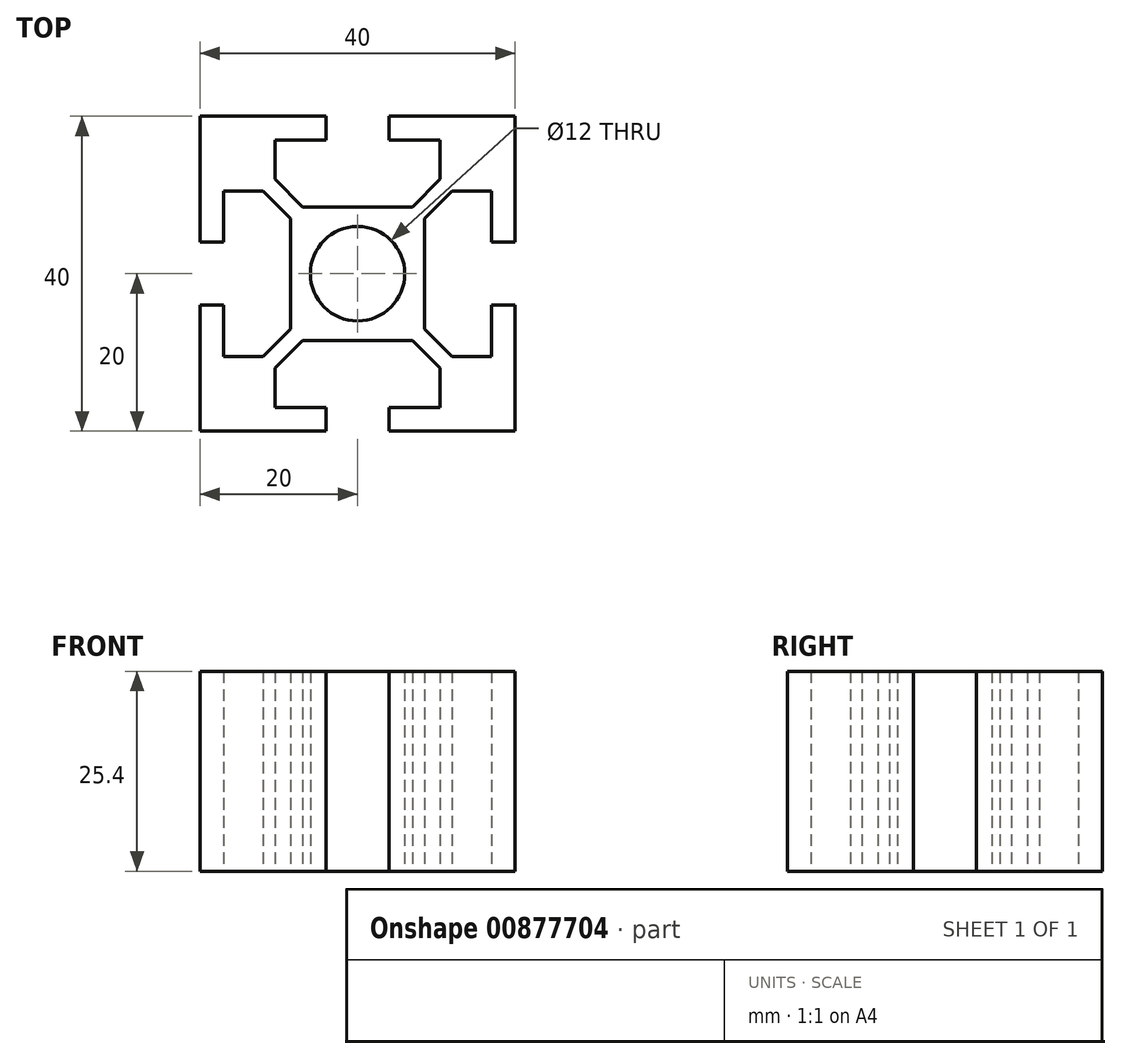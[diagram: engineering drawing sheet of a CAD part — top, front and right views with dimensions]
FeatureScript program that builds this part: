
annotation { "Feature Type Name" : "Feature", "Feature Type Description" : "" }
export const myFeature = defineFeature(function(context is Context, id is Id, definition is map)
    precondition{}
    {
        {
            var Q0;
            Q0=qCreatedBy(makeId("Top.planeOp"),FACE);
            var sketch = newSketch(context, id + "F0", { "sketchPlane" : qUnion([Q0])});
            skLineSegment(sketch, "E0", {"start": v(4, 17) * mm, "end": v(10.5, 17) * mm});
            skLineSegment(sketch, "E1", {"start": v(10.5, 17) * mm, "end": v(10.5, 12) * mm});
            skLineSegment(sketch, "E2", {"start": v(10.5, 12) * mm, "end": v(7, 8.5) * mm});
            skLineSegment(sketch, "E3", {"start": v(7, 8.5) * mm, "end": v(-7, 8.5) * mm});
            skLineSegment(sketch, "E4", {"start": v(-7, 8.5) * mm, "end": v(-10.5, 12) * mm});
            skLineSegment(sketch, "E5", {"start": v(-10.5, 12) * mm, "end": v(-10.5, 17) * mm});
            skLineSegment(sketch, "E6", {"start": v(-10.5, 17) * mm, "end": v(-4, 17) * mm});
            skLineSegment(sketch, "E7", {"start": v(-4, 17) * mm, "end": v(-4, 20) * mm});
            skLineSegment(sketch, "E8", {"start": v(-4, 20) * mm, "end": v(-20, 20) * mm});
            skLineSegment(sketch, "E9", {"start": v(-20, 20) * mm, "end": v(-20, 4) * mm});
            skLineSegment(sketch, "E10", {"start": v(-20, 4) * mm, "end": v(-17, 4) * mm});
            skLineSegment(sketch, "E11", {"start": v(-17, 4) * mm, "end": v(-17, 10.5) * mm});
            skLineSegment(sketch, "E12", {"start": v(-17, 10.5) * mm, "end": v(-12, 10.5) * mm});
            skLineSegment(sketch, "E13", {"start": v(-12, 10.5) * mm, "end": v(-8.5, 7) * mm});
            skLineSegment(sketch, "E14", {"start": v(-8.5, 7) * mm, "end": v(-8.5, -7) * mm});
            skLineSegment(sketch, "E15", {"start": v(-8.5, -7) * mm, "end": v(-12, -10.5) * mm});
            skLineSegment(sketch, "E16", {"start": v(-12, -10.5) * mm, "end": v(-17, -10.5) * mm});
            skLineSegment(sketch, "E17", {"start": v(-17, -10.5) * mm, "end": v(-17, -4) * mm});
            skLineSegment(sketch, "E18", {"start": v(-17, -4) * mm, "end": v(-20, -4) * mm});
            skLineSegment(sketch, "E19", {"start": v(-20, -4) * mm, "end": v(-20, -20) * mm});
            skLineSegment(sketch, "E20", {"start": v(-20, -20) * mm, "end": v(-4, -20) * mm});
            skLineSegment(sketch, "E21", {"start": v(-4, -20) * mm, "end": v(-4, -17) * mm});
            skLineSegment(sketch, "E22", {"start": v(-4, -17) * mm, "end": v(-10.5, -17) * mm});
            skLineSegment(sketch, "E23", {"start": v(-10.5, -17) * mm, "end": v(-10.5, -12) * mm});
            skLineSegment(sketch, "E24", {"start": v(-10.5, -12) * mm, "end": v(-7, -8.5) * mm});
            skLineSegment(sketch, "E25", {"start": v(-7, -8.5) * mm, "end": v(7, -8.5) * mm});
            skLineSegment(sketch, "E26", {"start": v(7, -8.5) * mm, "end": v(10.5, -12) * mm});
            skLineSegment(sketch, "E27", {"start": v(10.5, -12) * mm, "end": v(10.5, -17) * mm});
            skLineSegment(sketch, "E28", {"start": v(10.5, -17) * mm, "end": v(4, -17) * mm});
            skLineSegment(sketch, "E29", {"start": v(4, -17) * mm, "end": v(4, -20) * mm});
            skLineSegment(sketch, "E30", {"start": v(4, -20) * mm, "end": v(20, -20) * mm});
            skLineSegment(sketch, "E31", {"start": v(20, -20) * mm, "end": v(20, -4) * mm});
            skLineSegment(sketch, "E32", {"start": v(20, -4) * mm, "end": v(17, -4) * mm});
            skLineSegment(sketch, "E33", {"start": v(17, -4) * mm, "end": v(17, -10.5) * mm});
            skLineSegment(sketch, "E34", {"start": v(17, -10.5) * mm, "end": v(12, -10.5) * mm});
            skLineSegment(sketch, "E35", {"start": v(12, -10.5) * mm, "end": v(8.5, -7) * mm});
            skLineSegment(sketch, "E36", {"start": v(8.5, -7) * mm, "end": v(8.5, 7) * mm});
            skLineSegment(sketch, "E37", {"start": v(8.5, 7) * mm, "end": v(12, 10.5) * mm});
            skLineSegment(sketch, "E38", {"start": v(12, 10.5) * mm, "end": v(17, 10.5) * mm});
            skLineSegment(sketch, "E39", {"start": v(17, 10.5) * mm, "end": v(17, 4) * mm});
            skLineSegment(sketch, "E40", {"start": v(17, 4) * mm, "end": v(20, 4) * mm});
            skLineSegment(sketch, "E41", {"start": v(20, 4) * mm, "end": v(20, 20) * mm});
            skLineSegment(sketch, "E42", {"start": v(20, 20) * mm, "end": v(4, 20) * mm});
            skLineSegment(sketch, "E43", {"start": v(4, 20) * mm, "end": v(4, 17) * mm});
            skCircle(sketch, "E44", {"center": v(0, 0) * mm, "radius": 6 * mm});
            skSolve(sketch);
        }
        {
            var Q0;
            Q0=makeQuery(id+"F0.imprint","IMPRINT",FACE,{"disambiguationData":[TD([[makeQuery(id+"F0.imprint","IMPRINT",EDGE,{"derivedFrom":sQuery(id+"F0.wireOp",EDGE,"E0")}),1.0]])]});
            extrude(context, id + "F1", {"entities" : qUnion([Q0]), "depth" : 25.4 * mm, "offsetDistance" : 25.4 * mm});
        }
    });
